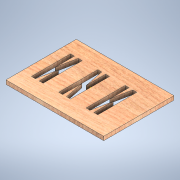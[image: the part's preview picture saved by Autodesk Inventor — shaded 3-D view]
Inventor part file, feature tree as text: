
AUTODESK INVENTOR PART (.ipt)
format: ipt  version: 2022 (Build 260153000, 153)  size: 178,176 bytes
history: native  units: mm
features: sketch x4, extrude x2, other x1
ambient origin geometry x8: Origin, YZ Plane, XZ Plane, XY Plane, X Axis, Y Axis, Z Axis, Center Point
bodies: Body1 (feature_tree)
feature tree (7):
  other  "Sólido1"
  sketch  "Boceto1"  dims[d0=250.0mm d1=180.0mm]
  extrude  "Extrusión1"  Depth=180.0mm
  sketch  "Boceto3"  dims[d4=30.0mm]
  extrude  "Extrusión2"  TaperAngle=0.0deg  [1 undecoded]
  sketch  "Boceto2"  dims[d2=10.0mm d3=0.0mm]
  sketch  "Boceto4"  dims[d5=0.0mm d6=10.0mm d7=100.0mm d8=10.0mm d10=100.0mm d11=100.0mm d12=10.0mm d13=100.0mm d14=20.0mm d15=20.0mm d16=10.0mm d17=0.0mm]
note: 1 required parameter value undecoded (feature->parameter linkage not recoverable at this tier; creation-order binding heuristic only, values carry confidence <= 0.55)
